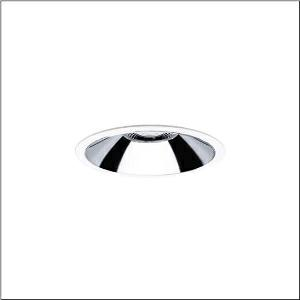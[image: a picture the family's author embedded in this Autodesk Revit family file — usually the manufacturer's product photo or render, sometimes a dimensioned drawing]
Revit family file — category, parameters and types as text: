
# Revit family: lunis_21_xl_51db15mf3d
name_source: partatom
category: Lighting Fixtures
units: mm (PartAtom-declared; Revit-internal decimal feet)

## family parameters
Cut with Voids When Loaded = No
Host = Face
Light Source = No
Part Type = Normal
Room Calculation Point = No
Round Connector Dimension = Use Diameter
Shared = No

## types (1)
- --- (1 x LED, 2620 lm, 23.5 W, 3000K)
    Apparent Load = 24 VA
    CIE Flux Codes = 89 99 100 100 100
    Color Rendering = 80
    Color Temperature = 3000K
    Default Elevation = 1800 mm
    Description = Lunis 21,  XL, downlight, of PC, light emission: direct distribution, LED rated luminous flux: 2.180lm, light colour: 830, control gear: ECG, with terminal, 3-pole, mains connection: 220..240V, AC, housing, round, of diecast aluminium, traffic white (RAL 9016), diameter: 213mm, protection rating (complete): IP20, protection rating (on room side): IP54, insulation class (complete): insulation class II (safety insulation), certification: CE, impact resistance: IK02, packaging unit: 1 piece
    Height = 0 mm  [stored 0 ft]
    Lamp = 1 x LED
    Lamp Light Flux = 2620 lm
    Lamp Power = 23.5 W
    Lamp count = 1
    Length = 213 mm
    Luminous efficacy = 111 lm/W
    Manufacturer = Siteco
    ModVariant = No
    Model = 51DB15MF3D
    Mounting Place = Ceiling
    Mounting Type = Recessed
    Number of Poles = 1
    OnlyDefault = Yes
    Power Factor = 1
    Product Name = Lunis 21 XL
    Product group = downlight
    ProductGroupID = 400
    Protection Class = Protection class II
    Protection Degree = IP 20
    RLX_Detail_Level = 1
    RLX_Emergency_Light_Flux = 0 lm
    RLX_Emergency_Type = 0
    RLX_Emergency_Type_DB = No
    RlxData = <blob elided: 27633 chars, md5=ba25fb1f>
    Socket = socket
    Standby Power = 0 W
    System Light Flux = 2620 lm
    System Power = 24 W
    Type Comments = factory setting: luminous flux: 100 % | (ON | ON)
    Type Image = l_1287385.jpg
    URL = http://relux.com
    VarID = @adj_101037
    Voltage = 0 V
    Weight = 0.00 kg
    Width = 0 mm  [stored 0 ft]

note: [stored X ft] marks values corroborated as IEEE doubles in the binary element streams (Revit-internal decimal feet)

## geometry (parser evidence)
native form markers: Blend x4, Sweep x12
no freeform markers — native parametric forms only
